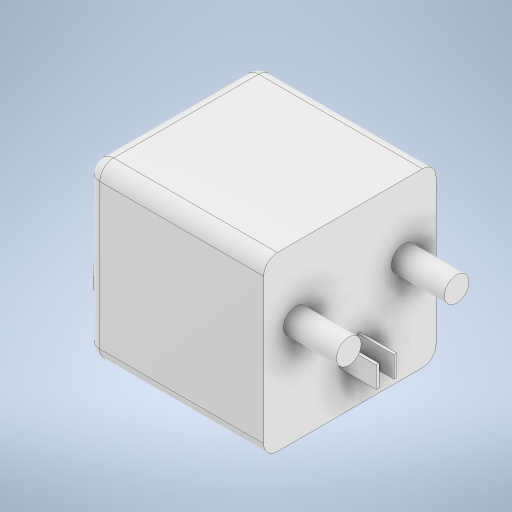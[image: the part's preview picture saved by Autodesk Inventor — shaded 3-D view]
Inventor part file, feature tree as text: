
AUTODESK INVENTOR PART (.ipt)
format: ipt  version: 2023 (Build 270158000, 158)  size: 324,096 bytes
history: native  units: in
note: dims shown in document units (in); Inventor stores cm internally (conversion verified against a paired STEP export)
features: extrude x4, sketch x2, fillet x2
ambient origin geometry x8: Origin, YZ Plane, XZ Plane, XY Plane, X Axis, Y Axis, Z Axis, Center Point
bodies: Solid1 (feature_tree)
feature tree (8):
  sketch  "Sketch1"  dims[d1=2.0472in d2=1.9882in]
  extrude  "Extrusion1"  Depth=1.9882in
  extrude  "Extrusion2"  Depth=0.1575in
  fillet  "Fillet1"  Radius=1.4409in
  sketch  "Sketch2"  dims[d3=0.563in d4=1.4409in d5=1.4409in d6=0.7283in d7=0.374in d8=0.4331in d9=0.4331in d10=0.8937in d11=0.2657in d12=0.3593in d14=0.1378in d15=0.0in d16=1.9882in d17=0.0in d18=0.1575in d19=0.2835in d20=0.2461in d21=0.0315in d22=0.4724in d23=0.876in d24=0.876in d25=1.2449in d26=0.3717in d27=1.9882in d28=0.7874in d29=0.7874in d30=0.6102in d31=0.0in d32=0.4232in d33=0.0in d34=0.1969in d35=0.8937in d36=0.1575in]
  extrude  "Extrusion3"  Depth=0.7283in
  extrude  "Extrusion4"  Depth=0.1575in
  fillet  "Fillet2"  Radius=0.4331in
